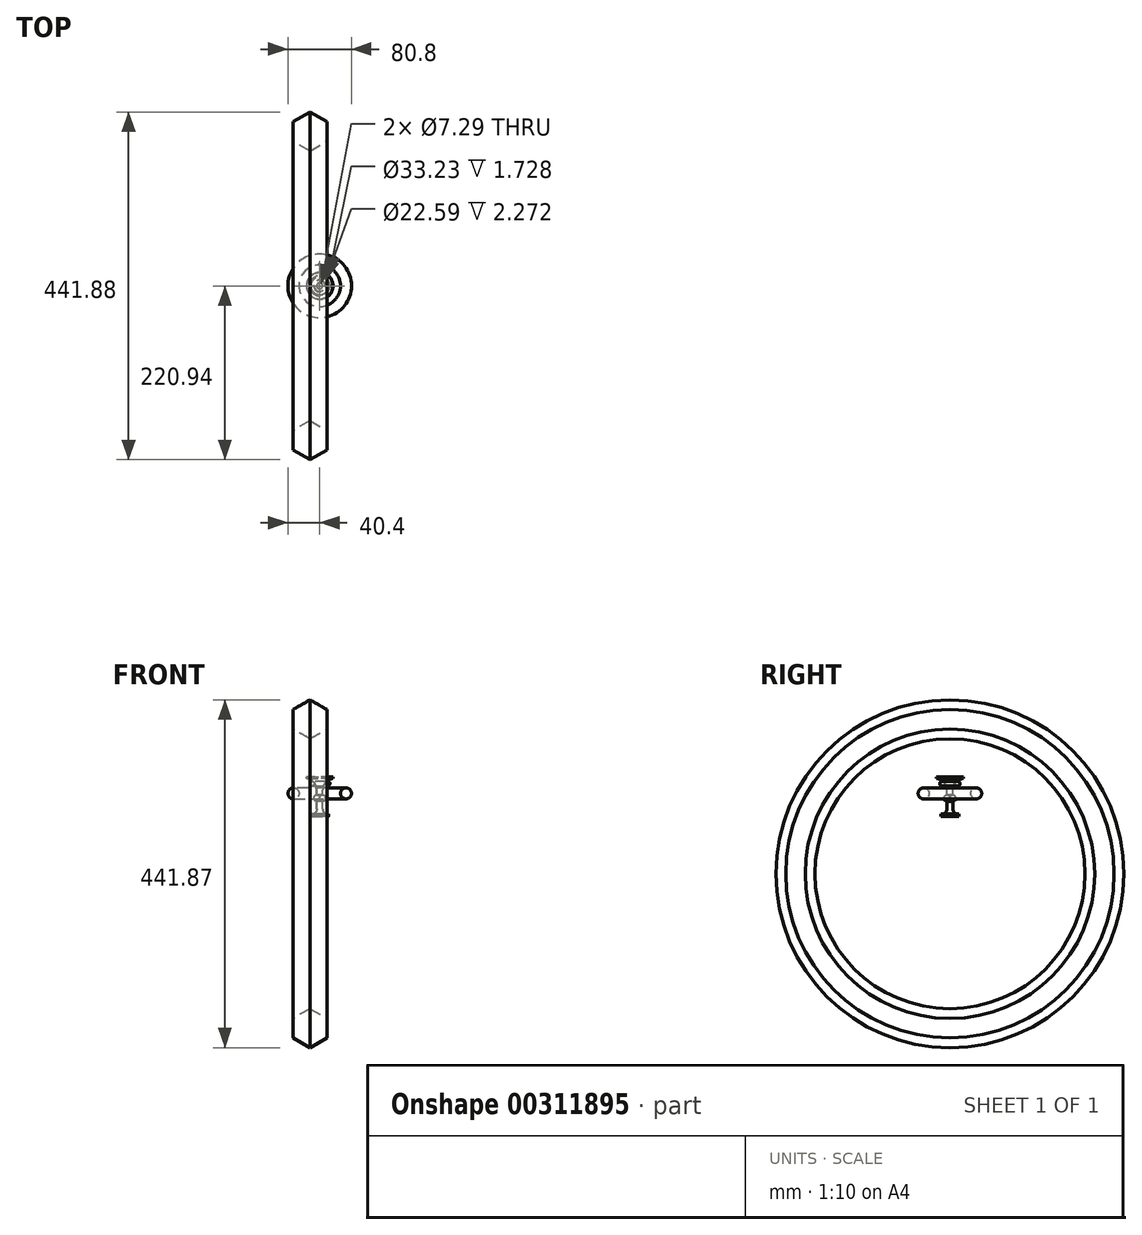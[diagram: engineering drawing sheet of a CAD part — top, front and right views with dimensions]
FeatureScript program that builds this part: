
annotation { "Feature Type Name" : "Feature", "Feature Type Description" : "" }
export const myFeature = defineFeature(function(context is Context, id is Id, definition is map)
    precondition{}
    {
        {
            var Q0;
            Q0=qCreatedBy(makeId("Right.planeOp"),FACE);
            var sketch = newSketch(context, id + "F0", { "sketchPlane" : qUnion([Q0])});
            skLineSegment(sketch, "E0", {"start": v(0, 0) * mm, "end": v(11.55, 0) * mm});
            skLineSegment(sketch, "E1", {"start": v(11.55, 0) * mm, "end": v(11.55, 2.78) * mm});
            skLineSegment(sketch, "E2", {"start": v(11.55, 2.78) * mm, "end": v(10.25, 2.78) * mm});
            skLineSegment(sketch, "E3", {"start": v(3.9, 9.13) * mm, "end": v(3.9, 19.2) * mm});
            skArc(sketch, "E4", {"start": v(3.9, 19.2) * mm, "mid": v(7.92, 23.22) * mm, "end": v(3.9, 27.24) * mm});
            skPoint(sketch, "E5.orphan", {"position": v(3.9, 14.89) * mm});
            skLineSegment(sketch, "E6", {"start": v(3.9, 27.24) * mm, "end": v(3.9, 33.74) * mm});
            skArc(sketch, "E7", {"start": v(16.87, 48.1) * mm, "mid": v(7.62, 43.42) * mm, "end": v(3.9, 33.74) * mm});
            skLineSegment(sketch, "E8", {"start": v(16.87, 48.1) * mm, "end": v(16.87, 50.06) * mm});
            skLineSegment(sketch, "E9", {"start": v(16.87, 50.06) * mm, "end": v(0, 50.06) * mm});
            skCircle(sketch, "E10", {"center": v(9.95, 41.64) * mm, "radius": 2.92 * mm});
            skPoint(sketch, "E11.visualSharp", {"position": v(3.9, 2.78) * mm});
            skArc(sketch, "E11.filletArc", {"start": v(3.9, 9.13) * mm, "mid": v(5.76, 4.64) * mm, "end": v(10.25, 2.78) * mm});
            skLineSegment(sketch, "E12", {"start": v(0, 50.06) * mm, "end": v(0, 0) * mm});
            skSolve(sketch);
        }
        {
            var Q0;
            Q0=makeQuery(id+"F0.imprint","IMPRINT",FACE,{"disambiguationData":[TD([[makeQuery(id+"F0.imprint","IMPRINT",EDGE,{"derivedFrom":sQuery(id+"F0.wireOp",EDGE,"E0")}),1.0]])]});
            var Q1;
            Q1=makeQuery(id+"F0.imprint","IMPRINT",FACE,{"disambiguationData":[TD([[makeQuery(id+"F0.imprint","IMPRINT",EDGE,{"derivedFrom":sQuery(id+"F0.wireOp",EDGE,"E10")}),1.0]])]});
            var Q2;
            Q2=sQuery(id+"F0.wireOp",EDGE,"E12");
            revolve(context, id + "F1", {"entities" : qUnion([Q0, Q1]), "axis" : qUnion([Q2]), "revolveType" : RevolveType.FULL});
        }
        {
            var Q0;
            Q0=makeQuery(id+"F1.opRevolve","SWEPT_FACE",FACE,{"disambiguationData":[OSD([sQuery(id+"F0.wireOp",EDGE,"E9")])]});
            shell(context, id + "F2", {"entities" : qUnion([Q0]), "thickness" : 0.25 * mm});
        }
        {
            var Q0;
            Q0=qCreatedBy(makeId("Front.planeOp"),FACE);
            var sketch = newSketch(context, id + "F3", { "sketchPlane" : qUnion([Q0])});
            skCircle(sketch, "E13", {"center": v(33.39, 29.18) * mm, "radius": 7.02 * mm});
            skLineSegment(sketch, "E14", {"start": v(-18.65, -7.22) * mm, "end": v(18.05, -7.22) * mm});
            skLineSegment(sketch, "E15.0", {"start": v(0, 50.06) * mm, "end": v(0, 0) * mm});
            skSolve(sketch);
        }
        {
            var Q0;
            Q0=makeQuery(id+"F3.imprint","IMPRINT",FACE,{"disambiguationData":[TD([[makeQuery(id+"F3.imprint","IMPRINT",EDGE,{"derivedFrom":sQuery(id+"F3.wireOp",EDGE,"E13")}),1.0]])]});
            var Q1;
            Q1=sQuery(id+"F3.wireOp",EDGE,"E15.0");
            revolve(context, id + "F4", {"entities" : qUnion([Q0]), "axis" : qUnion([Q1]), "revolveType" : RevolveType.FULL});
        }
        {
            var Q0;
            Q0=qCreatedBy(makeId("Front.planeOp"),FACE);
            var sketch = newSketch(context, id + "F5", { "sketchPlane" : qUnion([Q0])});
            skLineSegment(sketch, "E16", {"start": v(-29.11, -72.9) * mm, "end": v(65.46, -72.9) * mm});
            skCircle(sketch, "E17.cCircle", {"center": v(-12.36, 123.28) * mm, "radius": 21.44 * mm, "construction": true});
            skLineSegment(sketch, "E17.0", {"start": v(9.08, 135.66) * mm, "end": v(9.08, 110.9) * mm});
            skLineSegment(sketch, "E17.1", {"start": v(9.08, 110.9) * mm, "end": v(-12.36, 98.52) * mm});
            skLineSegment(sketch, "E17.2", {"start": v(-12.36, 98.52) * mm, "end": v(-33.8, 110.9) * mm});
            skLineSegment(sketch, "E17.3", {"start": v(-33.8, 110.9) * mm, "end": v(-33.8, 135.66) * mm});
            skLineSegment(sketch, "E17.4", {"start": v(-33.8, 135.66) * mm, "end": v(-12.36, 148.03) * mm});
            skLineSegment(sketch, "E17.5", {"start": v(-12.36, 148.03) * mm, "end": v(9.08, 135.66) * mm});
            skPoint(sketch, "E17.0.midPoint", {"position": v(9.08, 123.28) * mm});
            skSolve(sketch);
        }
        {
            var Q0;
            Q0=makeQuery(id+"F5.imprint","IMPRINT",FACE,{"disambiguationData":[TD([[makeQuery(id+"F5.imprint","IMPRINT",EDGE,{"derivedFrom":sQuery(id+"F5.wireOp",EDGE,"E17.0")}),-1.0]])]});
            var Q1;
            Q1=sQuery(id+"F5.wireOp",EDGE,"E16");
            revolve(context, id + "F6", {"entities" : qUnion([Q0]), "axis" : qUnion([Q1]), "revolveType" : RevolveType.FULL});
        }
    });
